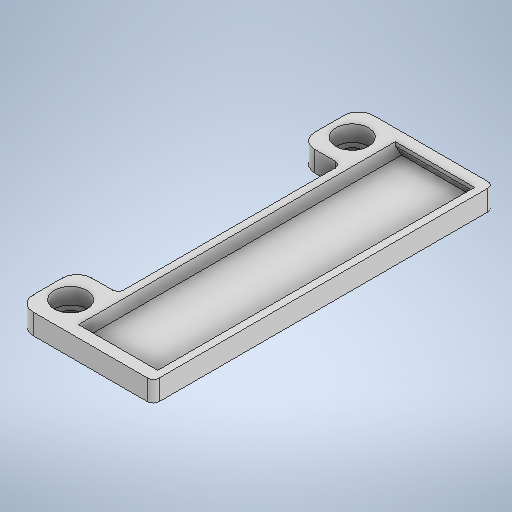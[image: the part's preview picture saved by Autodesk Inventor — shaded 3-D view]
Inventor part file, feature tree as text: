
AUTODESK INVENTOR PART (.ipt)
format: ipt  version: 2025 (Build 290162000, 162)  size: 329,216 bytes
history: native  units: mm
features: extrude x4, sketch x4, hole x1, fillet x1
ambient origin geometry x8: Origin, YZ Plane, XZ Plane, XY Plane, X Axis, Y Axis, Z Axis, Center Point
bodies: Solid1 (feature_tree)
feature tree (10):
  extrude  "Extrusion1"  Depth=116.0mm
  extrude  "Extrusion2"  TaperAngle=60.0deg  [1 undecoded]
  extrude  "Extrusion3"  Depth=5.0mm
  sketch  "Sketch5"  dims[d8=106.5mm d9=116.0mm d10=4.75mm d11=7.0mm d12=0.0mm d13=2.5mm d14=2.5mm d15=10.0mm d16=0.0mm d17=4.0mm d18=4.0mm d19=20.0mm d20=14.0mm d21=22.2mm d22=10.0mm d23=6.2mm d24=0.0mm d25=0.0mm d26=6.756mm d27=12.7mm d28=11.113mm d29=5.5mm d30=90.0deg d31=19.05mm d32=20.594885mm d33=5.0mm d34=2.0mm]
  extrude  "Extrusion4"  Depth=116.0mm
  hole  "Hole1"  [1 undecoded]
  fillet  "Fillet1"  Radius=7.0mm
  sketch  "Sketch1"  dims[d0=32.0mm d1=116.0mm]
  sketch  "Sketch3"  dims[d2=7.0mm d3=0.0mm d4=60.0deg]
  sketch  "Sketch4"  dims[d6=60.0deg d7=5.0mm]
note: 2 required parameter values undecoded (feature->parameter linkage not recoverable at this tier; creation-order binding heuristic only, values carry confidence <= 0.55)
